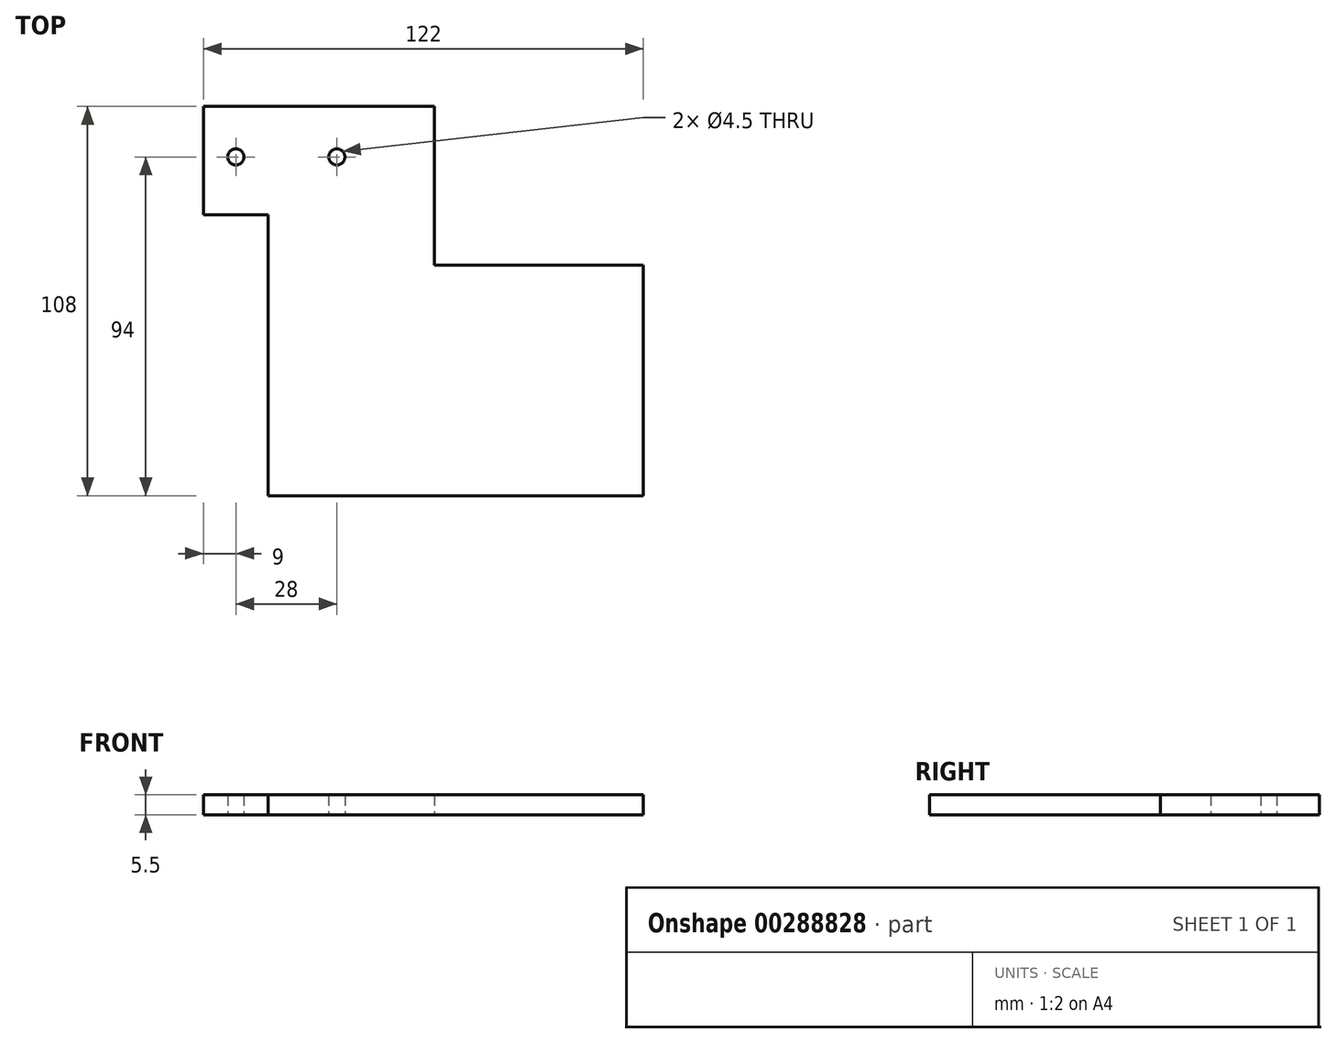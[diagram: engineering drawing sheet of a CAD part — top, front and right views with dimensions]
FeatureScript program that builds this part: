
annotation { "Feature Type Name" : "Feature", "Feature Type Description" : "" }
export const myFeature = defineFeature(function(context is Context, id is Id, definition is map)
    precondition{}
    {
        {
            var Q0;
            Q0=qCreatedBy(makeId("Top.planeOp"),FACE);
            var sketch = newSketch(context, id + "F0", { "sketchPlane" : qUnion([Q0])});
            skLineSegment(sketch, "E0", {"start": v(0, 0) * mm, "end": v(0, 44) * mm});
            skLineSegment(sketch, "E1", {"start": v(0, 44) * mm, "end": v(-64, 44) * mm});
            skLineSegment(sketch, "E2", {"start": v(-64, 44) * mm, "end": v(-64, 14) * mm});
            skLineSegment(sketch, "E3", {"start": v(-64, 14) * mm, "end": v(-46, 14) * mm});
            skLineSegment(sketch, "E4", {"start": v(-46, 14) * mm, "end": v(-46, -64) * mm});
            skLineSegment(sketch, "E5", {"start": v(-46, -64) * mm, "end": v(58, -64) * mm});
            skLineSegment(sketch, "E6", {"start": v(58, -64) * mm, "end": v(58, 0) * mm});
            skLineSegment(sketch, "E7", {"start": v(58, 0) * mm, "end": v(0, 0) * mm});
            skCircle(sketch, "E8", {"center": v(-55, 30) * mm, "radius": 2.25 * mm});
            skCircle(sketch, "E9", {"center": v(-27, 30) * mm, "radius": 2.25 * mm});
            skLineSegment(sketch, "E10", {"start": v(-27, 30) * mm, "end": v(-55, 30) * mm, "construction": true});
            skSolve(sketch);
        }
        {
            var Q0;
            Q0 = qSketchRegion(id + "F0", true);
            extrude(context, id + "F1", {"entities" : qUnion([Q0]), "depth" : 5.5 * mm});
        }
    });
